# Revit family: Plumbing-Flushometer-Sloan-Valve-CX-8198_
name_source: partatom
category: Plumbing Fixtures
units: mm (PartAtom-declared; Revit-internal decimal feet)

## family parameters
Cut with Voids When Loaded = Yes
Host = Face
Maintain Annotation Orientation = No
OmniClass Number = 23.45.05.14.99
OmniClass Title = Other Sanitary Washing Plumbing Fixtures
Part Type = Normal
Room Calculation Point = No
Round Connector Dimension = Use Diameter
Shared = No

## types (2) — shared parameters
Apparent Load = 0 VA
Assembly Code = D2020300
CW Connection = Yes
Current = 0 A
Date Updated = 09.12.2024
Default Elevation = 0"
Edition number = 1
HW Connection = No
Height = 6 1/4"
Keynote = 15410
Manufacturer = Sloan Valve
Number of Poles = 1
Operating Water Pressure = 20 – 80 PSI (138 – 552 kPa)
Power Factor = 1
Product Material = Sloan Valve - Finish - Brushed Brass
Product data url = https://bimobject.com
URL = www.sloanvalve.com
Valve Pressure Drop = 0.00 psi
Vent Connection = No
Version = 2
Voltage = 6 V
Waste Connection = No
Water Inlet Connection Diameter = 2"
Water Outlet Connection Diameter = 2"
zero-valued in all types: CWFU, HWFU, WFU

## per-type parameters (varying)
| type | Description | Flush Rate | Part Number |
| CX 8198-0.5-PVDBB | 0.5 gpf, Filtered, Brushed Brass Finish, Fixture Connection Rear Spud, Single Flush, Integrated Control Stop, 3.25-4.25 L Dimension, Adjustable Flush Connection Outlet Tube, Electrical Override, Battery with Hardwired Option, Sensor-Operated, Short V500A & Adjustable Flush Connection Vacuum Breaker, Front Accessible Wall Box | 0.5 gpf (1.9 Lpf) | 34003017 |
| CX 8198-0.25-PVDBB | 0.25 gpf, Filtered, Brushed Brass Finish, Fixture Connection Rear Spud, Single Flush, Integrated Control Stop, 3.25-4.25 L Dimension, Adjustable Flush Connection Outlet Tube, Electrical Override, Battery with Hardwired Option, Sensor-Operated, Short V500A & Adjustable Flush Connection Vacuum Breaker, Front Accessible Wall Box | 0.25 gpf (0.9 Lpf) | 34003016 |

note: column(s) folded — value = type name in every type: Model

## geometry (parser evidence)
native form markers: Sweep x4
no freeform markers — native parametric forms only
